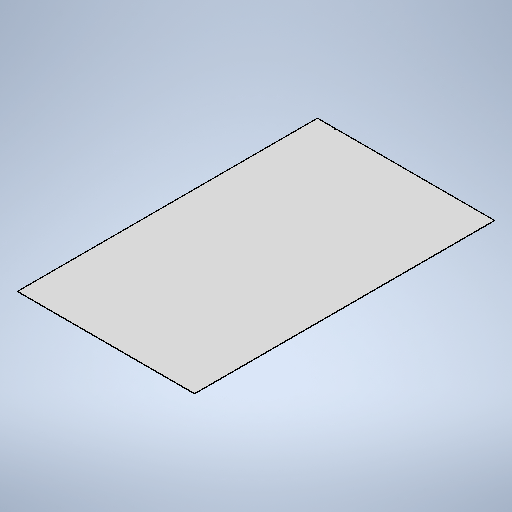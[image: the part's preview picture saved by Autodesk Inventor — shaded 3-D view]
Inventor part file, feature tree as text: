
AUTODESK INVENTOR PART (.ipt)
format: ipt  version: 2025.3 (Build 293356000, 356)  size: 299,520 bytes
history: native  units: mm
features: other x3, sketch x2, sheet_metal_op x1
ambient origin geometry x8: Origin, YZ Plane, XZ Plane, XY Plane, X Axis, Y Axis, Z Axis, Center Point
bodies: Solid1 (feature_tree)
feature tree (6):
  sheet_metal_op  "Face1"
  sketch  "Sketch1"  dims[d2=3.0mm]
  other  "Plate1"
  sketch  "Sketch5"  dims[d22=1240.0mm d23=2100.0mm d24=35.0mm d25=35.0mm d28=90.0mm d29=970.0mm d30=2.0mm d31=5.0mm d32=0.5mm d33=3.0mm d34=2.0mm d35=5.0mm d36=3.0mm d37=5.0mm d38=100.0mm d39=3.0mm d40=0.0mm]
  other  "Cut1"
  other  "Definition1"
